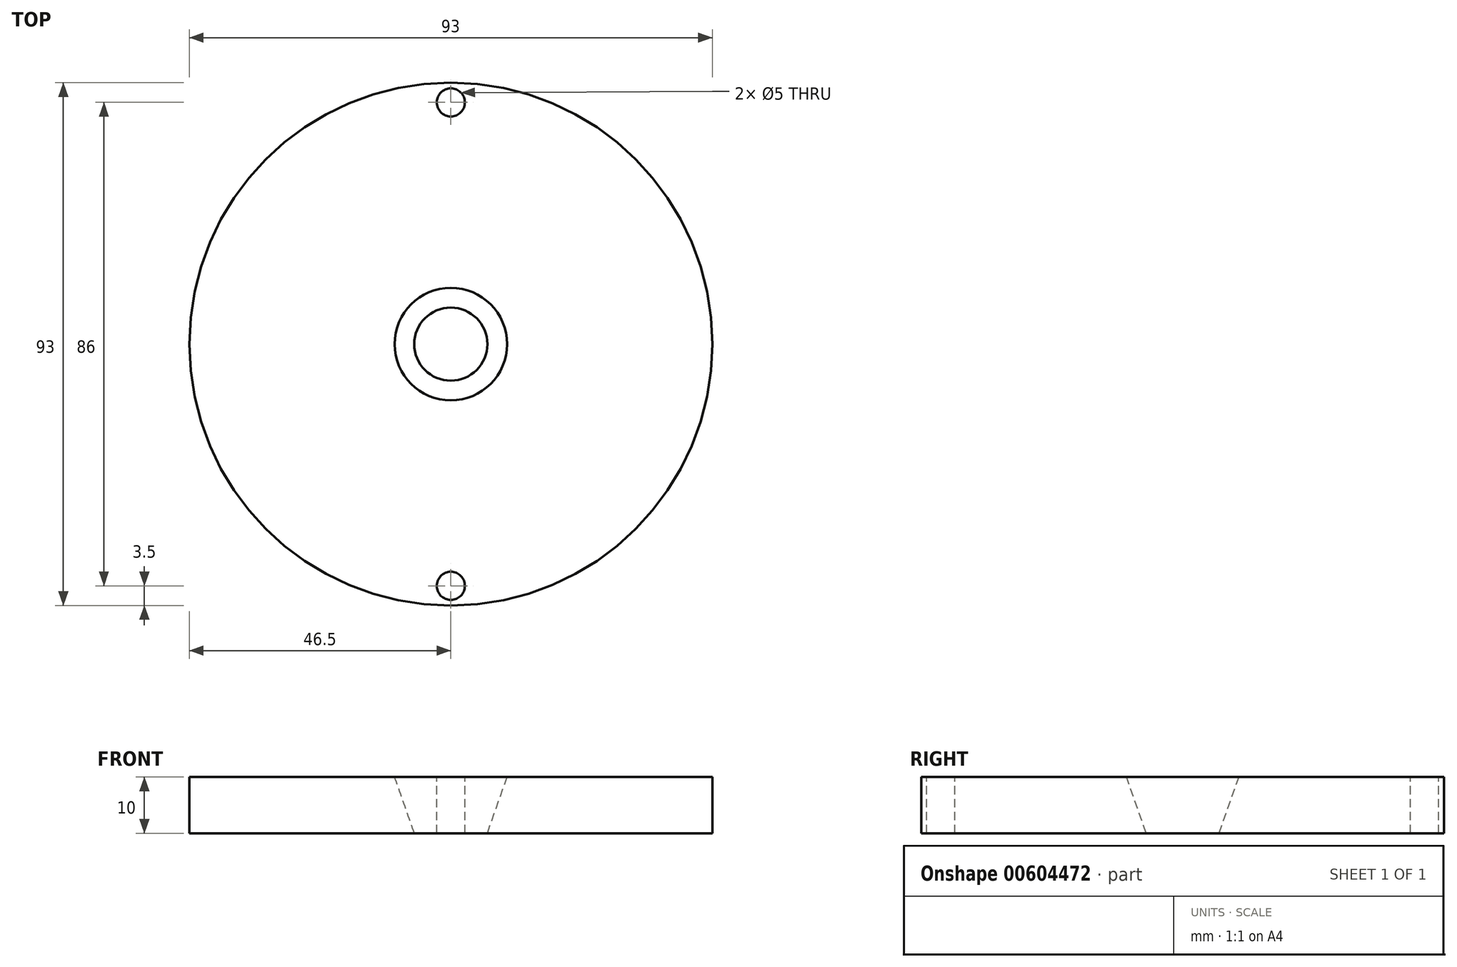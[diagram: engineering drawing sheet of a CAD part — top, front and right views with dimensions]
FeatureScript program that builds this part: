
annotation { "Feature Type Name" : "Feature", "Feature Type Description" : "" }
export const myFeature = defineFeature(function(context is Context, id is Id, definition is map)
    precondition{}
    {
        {
            var Q0;
            Q0=qCreatedBy(makeId("Front.planeOp"),FACE);
            var sketch = newSketch(context, id + "F0", { "sketchPlane" : qUnion([Q0])});
            skLineSegment(sketch, "E0", {"start": v(46.5, 0) * mm, "end": v(46.5, 10) * mm});
            skLineSegment(sketch, "E1", {"start": v(10, 10) * mm, "end": v(6.5, 0) * mm});
            skLineSegment(sketch, "E2", {"start": v(46.5, 10) * mm, "end": v(10, 10) * mm});
            skLineSegment(sketch, "E3", {"start": v(6.5, 0) * mm, "end": v(46.5, 0) * mm});
            skLineSegment(sketch, "E4", {"start": v(0, 0) * mm, "end": v(0, 12.57) * mm});
            skSolve(sketch);
        }
        {
            var Q0;
            Q0=makeQuery(id+"F0.imprint","IMPRINT",FACE,{"disambiguationData":[TD([[makeQuery(id+"F0.imprint","IMPRINT",EDGE,{"derivedFrom":sQuery(id+"F0.wireOp",EDGE,"E0")}),1.0]])]});
            var Q1;
            Q1=sQuery(id+"F0.wireOp",EDGE,"E4");
            revolve(context, id + "F1", {"entities" : qUnion([Q0]), "axis" : qUnion([Q1]), "revolveType" : RevolveType.FULL});
        }
        {
            var Q0;
            Q0=makeQuery(id+"F1.opRevolve","SWEPT_FACE",FACE,{"disambiguationData":[OSD([sQuery(id+"F0.wireOp",EDGE,"E2")])]});
            var sketch = newSketch(context, id + "F2", { "sketchPlane" : qUnion([Q0])});
            skCircle(sketch, "E5", {"center": v(0, -43) * mm, "radius": 2.5 * mm});
            skCircle(sketch, "E6", {"center": v(0, 43) * mm, "radius": 2.5 * mm});
            skSolve(sketch);
        }
        {
            var Q0;
            Q0=sQuery(id+"F2.wireOp",VERTEX,"E5.center");
            var Q1;
            Q1=sQuery(id+"F2.wireOp",VERTEX,"E6.center");
            var Q2;
            Q2=makeQuery(id+"F1.opRevolve","SWEPT_BODY",BODY,{"disambiguationData":[OSD([sQuery(id+"F0.wireOp",EDGE,"E0"),sQuery(id+"F0.wireOp",EDGE,"E1"),sQuery(id+"F0.wireOp",EDGE,"E2"),sQuery(id+"F0.wireOp",EDGE,"E3")])]});
            hole(context, id + "F3", {"style" : HoleStyle.SIMPLE, "endStyle" : HoleEndStyle.THROUGH, "holeDiameter" : 5 * mm, "majorDiameter" : 5 * mm, "isTappedThrough" : true, "tappedDepth" : 12 * mm, "tapClearance" : 3, "locations" : qUnion([Q0, Q1]), "scope" : qUnion([Q2])});
        }
    });
